# Revit family: VICTRIX PRO 150 V2
name_source: partatom
category: Apparecchi idraulici
units: mm (PartAtom-declared; Revit-internal decimal feet)

## family parameters
Condiviso = No
Host = Muro
Numero OmniClass = 23.45.00.00
Punto di calcolo locali = No
Quota connettore circolare = Usa diametro
Sempre verticale = Sì
Taglio con vuoti quando caricato = No
Tipo di parte = Normale
Titolo OmniClass = Sanitary, Laundry, and Cleaning Equipment

## types (1)
- VICTRIX PRO 150 V2
    Alimentazione elettrica = 230 - 50
230 - 50
    Alimentazione gas = METANO - GPL
    Assorbimento nominale A = 3,2
    Codice = 3.033855
    Collegamenti alimentazione gas = 1"
    Collegamenti idraulici impianto = 1" 1/2
    Contenuto acqua di caldaia = 12
    Description_en = Wall-hung light commercial condensing gas boiler
    Description_it = Caldaia murale modulare a condensazione, ad alta potenza
    Diametro ingresso aria = 100
    Diametro uscita fumisteria = 110 mm  [stored 0.360892 ft]
    Grado isolamento elettrico IP = X5D
    Mass = 112.00 kg
    Name_en = VICTRIX PRO 150 V2
    Name_it = VICTRIX PRO 150 V2
    Overall Depth = 627 mm  [stored 2.05709 ft]
    Overall Height = 1098 mm  [stored 3.60236 ft]
    Overall Width = 600 mm
    Portata gas al bruciatore (min / Max) GPL - kg/h = 2,25 - 10,95
    Portata gas al bruciatore (min / Max) Metano m3/h = 3,07 - 14,92
    Portata termica nominale massima kW (kcal/h) = 141
    Potenza elettrica installata W = 580
    Potenza utile nominale massima (80/60°C) kW (kcal/h) = 138,3
    Potenza utile nominale minima (80/60°C) kW (kcal/h) = 28,3
    Pressione massima d'esercizio impianto - bar = 6
    Prospetto di default = 0 mm  [stored 0 ft]
    Rendimento al 100% Pn (80/60°C) = 98.1
    Rendimento al 30% Pn (80/60°C) = 0
    Temperatura massima d'esercizio impianto = 95 °C
    Temperatura regolabile impianto di riscaldamento = 15-90

note: [stored X ft] marks values corroborated as IEEE doubles in the binary element streams (Revit-internal decimal feet)
